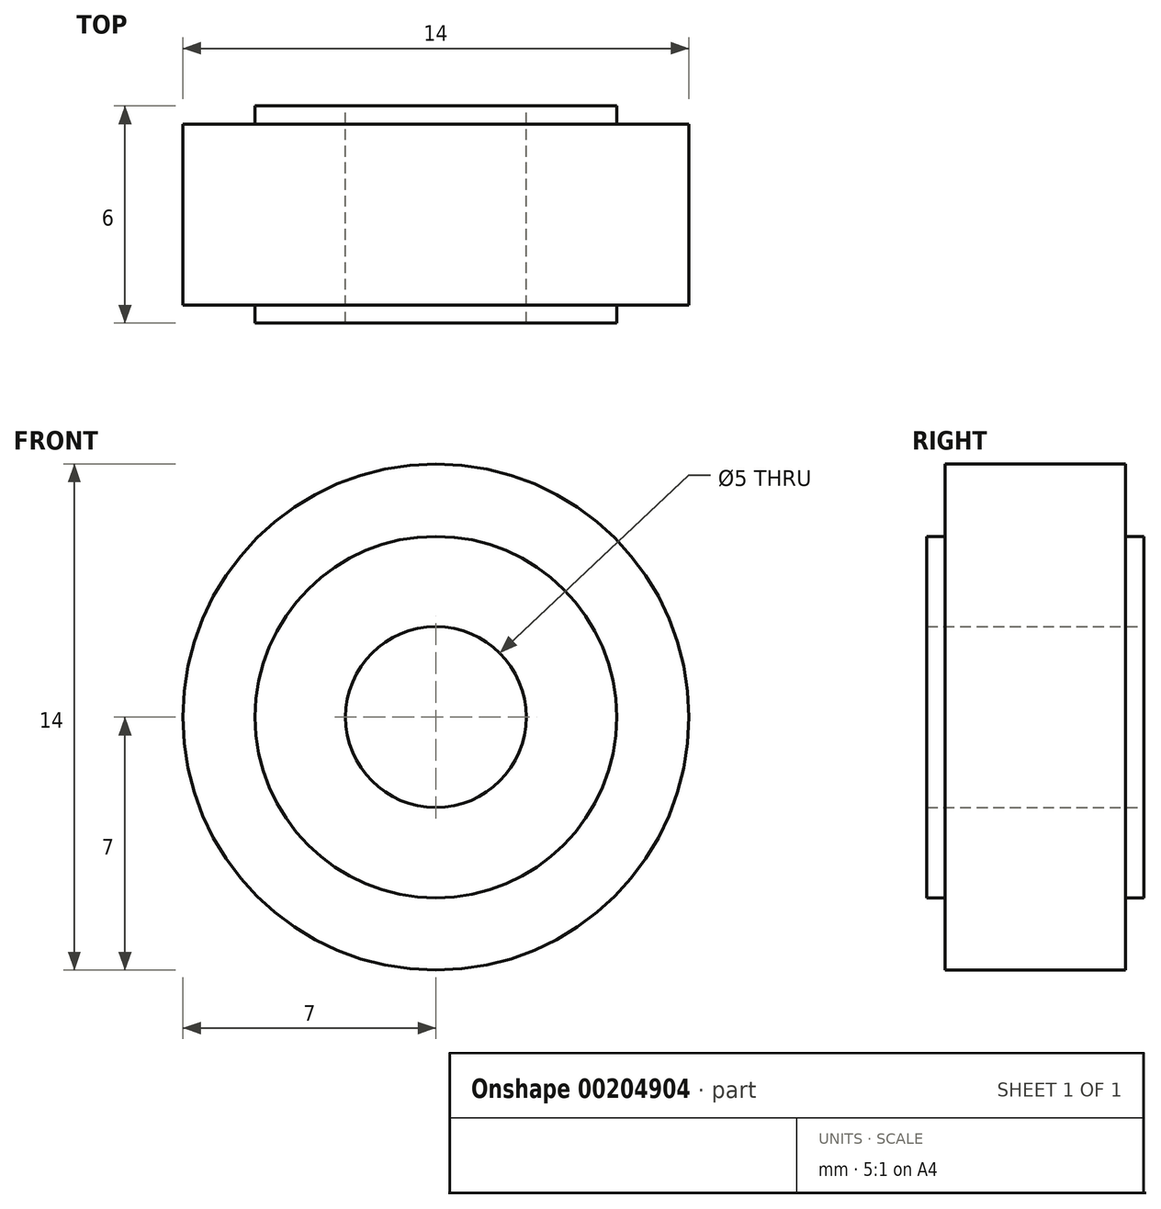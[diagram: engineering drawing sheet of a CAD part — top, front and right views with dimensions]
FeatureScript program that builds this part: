
annotation { "Feature Type Name" : "Feature", "Feature Type Description" : "" }
export const myFeature = defineFeature(function(context is Context, id is Id, definition is map)
    precondition{}
    {
        {
            var Q0;
            Q0=qCreatedBy(makeId("Front.planeOp"),FACE);
            var sketch = newSketch(context, id + "F0", { "sketchPlane" : qUnion([Q0])});
            skCircle(sketch, "E0", {"center": v(0, 0) * mm, "radius": 7 * mm});
            skCircle(sketch, "E1", {"center": v(0, 0) * mm, "radius": 2.5 * mm});
            skSolve(sketch);
        }
        {
            var Q0;
            Q0=makeQuery(id+"F0.imprint","IMPRINT",FACE,{"disambiguationData":[TD([[makeQuery(id+"F0.imprint","IMPRINT",EDGE,{"derivedFrom":sQuery(id+"F0.wireOp",EDGE,"E0")}),1.0]])]});
            extrude(context, id + "F1", {"entities" : qUnion([Q0]), "depth" : 5 * mm});
        }
        {
            var Q0;
            Q0=makeQuery(id+"F1.opExtrude","CAP_FACE",FACE,{"disambiguationData":[OSD([sQuery(id+"F0.wireOp",EDGE,"E0"),sQuery(id+"F0.wireOp",EDGE,"E1")])],"isStart":false});
            var sketch = newSketch(context, id + "F2", { "sketchPlane" : qUnion([Q0])});
            skCircle(sketch, "E2", {"center": v(0, 0) * mm, "radius": 5 * mm});
            skCircle(sketch, "E3", {"center": v(0, 0) * mm, "radius": 2.5 * mm});
            skSolve(sketch);
        }
        {
            var Q0;
            Q0=makeQuery(id+"F2.imprint","IMPRINT",FACE,{"disambiguationData":[TD([[makeQuery(id+"F2.imprint","IMPRINT",EDGE,{"derivedFrom":sQuery(id+"F2.wireOp",EDGE,"E2")}),1.0]])]});
            extrude(context, id + "F3", {"entities" : qUnion([Q0]), "operationType" : NewBodyOperationType.ADD, "depth" : .5 * mm});
        }
        {
            var Q0;
            Q0=makeQuery(id+"F1.opExtrude","CAP_FACE",FACE,{"disambiguationData":[OSD([sQuery(id+"F0.wireOp",EDGE,"E0"),sQuery(id+"F0.wireOp",EDGE,"E1")])],"isStart":true});
            var sketch = newSketch(context, id + "F4", { "sketchPlane" : qUnion([Q0])});
            skCircle(sketch, "E4", {"center": v(0, 0) * mm, "radius": 2.5 * mm});
            skCircle(sketch, "E5", {"center": v(0, 0) * mm, "radius": 5 * mm});
            skSolve(sketch);
        }
        {
            var Q0;
            Q0=makeQuery(id+"F4.imprint","IMPRINT",FACE,{"disambiguationData":[TD([[makeQuery(id+"F4.imprint","IMPRINT",EDGE,{"derivedFrom":sQuery(id+"F4.wireOp",EDGE,"E4")}),1.0]])]});
            extrude(context, id + "F5", {"entities" : qUnion([Q0]), "operationType" : NewBodyOperationType.ADD, "depth" : .5 * mm});
        }
    });
